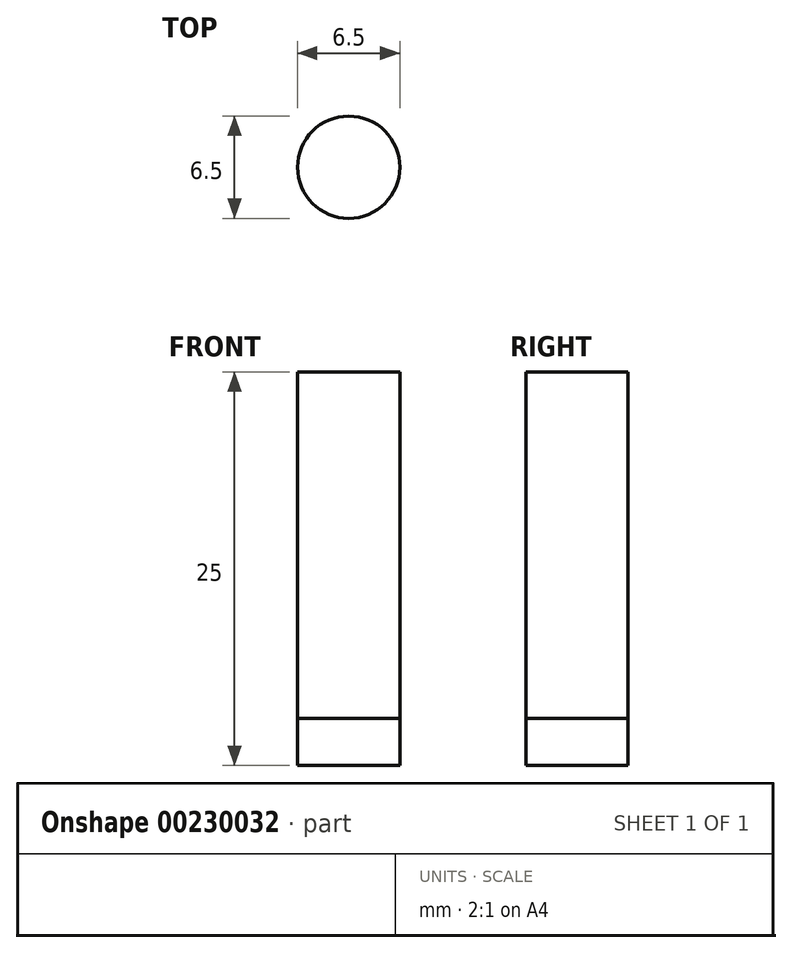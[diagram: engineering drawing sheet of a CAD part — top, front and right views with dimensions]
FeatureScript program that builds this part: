
annotation { "Feature Type Name" : "Feature", "Feature Type Description" : "" }
export const myFeature = defineFeature(function(context is Context, id is Id, definition is map)
    precondition{}
    {
        {
            var Q0;
            Q0=qCreatedBy(makeId("Top.planeOp"),FACE);
            var sketch = newSketch(context, id + "F0", { "sketchPlane" : qUnion([Q0])});
            skLineSegment(sketch, "E0", {"start": v(0, 0) * mm, "end": v(0, 7) * mm});
            skLineSegment(sketch, "E1", {"start": v(0, 7) * mm, "end": v(3, 7) * mm});
            skLineSegment(sketch, "E2", {"start": v(3, 7) * mm, "end": v(3, 17) * mm});
            skPoint(sketch, "E3.start.orphan", {"position": v(0, 17.47) * mm});
            skLineSegment(sketch, "E4", {"start": v(0, 17) * mm, "end": v(3, 17) * mm});
            skLineSegment(sketch, "E5", {"start": v(0, 17) * mm, "end": v(0, 24) * mm});
            skLineSegment(sketch, "E6", {"start": v(3, 24) * mm, "end": v(0, 24) * mm});
            skLineSegment(sketch, "E7", {"start": v(3, 24) * mm, "end": v(3, 34) * mm});
            skLineSegment(sketch, "E8", {"start": v(3, 34) * mm, "end": v(0, 34) * mm});
            skLineSegment(sketch, "E9", {"start": v(0, 34) * mm, "end": v(0, 41) * mm});
            skLineSegment(sketch, "E10", {"start": v(0, 41) * mm, "end": v(-17, 41) * mm});
            skLineSegment(sketch, "E11", {"start": v(-17, 44) * mm, "end": v(-17, 41) * mm});
            skLineSegment(sketch, "E12", {"start": v(-27, 44) * mm, "end": v(-17, 44) * mm});
            skLineSegment(sketch, "E13", {"start": v(-27, 41) * mm, "end": v(-27, 44) * mm});
            skLineSegment(sketch, "E14", {"start": v(-47, 41) * mm, "end": v(-27, 41) * mm});
            skLineSegment(sketch, "E15", {"start": v(-47, 41) * mm, "end": v(-47, 44) * mm});
            skLineSegment(sketch, "E16", {"start": v(-47, 44) * mm, "end": v(-57, 44) * mm});
            skLineSegment(sketch, "E17", {"start": v(-57, 44) * mm, "end": v(-57, 41) * mm});
            skLineSegment(sketch, "E18", {"start": v(-57, 41) * mm, "end": v(-77, 41) * mm});
            skLineSegment(sketch, "E19", {"start": v(-77, 41) * mm, "end": v(-77, 44) * mm});
            skLineSegment(sketch, "E20", {"start": v(-77, 44) * mm, "end": v(-87, 44) * mm});
            skLineSegment(sketch, "E21", {"start": v(-87, 44) * mm, "end": v(-87, 41) * mm});
            skLineSegment(sketch, "E22", {"start": v(-87, 41) * mm, "end": v(-104, 41) * mm});
            skLineSegment(sketch, "E23", {"start": v(-17, 0) * mm, "end": v(0, 0) * mm});
            skLineSegment(sketch, "E24", {"start": v(-17, -3) * mm, "end": v(-17, 0) * mm});
            skLineSegment(sketch, "E25", {"start": v(-27, -3) * mm, "end": v(-17, -3) * mm});
            skLineSegment(sketch, "E26", {"start": v(-27, 0) * mm, "end": v(-27, -3) * mm});
            skPoint(sketch, "E27.start.orphan", {"position": v(-47, 0) * mm});
            skLineSegment(sketch, "E28", {"start": v(-47, 0) * mm, "end": v(-27, 0) * mm});
            skLineSegment(sketch, "E29", {"start": v(-47, -3) * mm, "end": v(-47, 0) * mm});
            skLineSegment(sketch, "E30", {"start": v(-57, -3.09) * mm, "end": v(-47, -3) * mm});
            skPoint(sketch, "E31.start.orphan", {"position": v(-77, 0) * mm});
            skPoint(sketch, "E32.start.orphan", {"position": v(-57.64, 0) * mm});
            skPoint(sketch, "E33.start.orphan", {"position": v(-57.64, -3) * mm});
            skLineSegment(sketch, "E34", {"start": v(-57, 0) * mm, "end": v(-57.64, 0) * mm});
            skLineSegment(sketch, "E35", {"start": v(-57, 0) * mm, "end": v(-57, -3) * mm});
            skLineSegment(sketch, "E36", {"start": v(-57, 0) * mm, "end": v(-77, 0) * mm});
            skLineSegment(sketch, "E37", {"start": v(-77, -3.09) * mm, "end": v(-77, 0) * mm});
            skLineSegment(sketch, "E38", {"start": v(-87, -3) * mm, "end": v(-77, -3.09) * mm});
            skLineSegment(sketch, "E39", {"start": v(-87.03, 0) * mm, "end": v(-87, -3) * mm});
            skLineSegment(sketch, "E40", {"start": v(-104.03, 0) * mm, "end": v(-87.03, 0) * mm});
            skLineSegment(sketch, "E41", {"start": v(-104.03, 0) * mm, "end": v(-104.03, 7) * mm});
            skLineSegment(sketch, "E42", {"start": v(-104.03, 7) * mm, "end": v(-107.03, 7) * mm});
            skLineSegment(sketch, "E43", {"start": v(-107.03, 7) * mm, "end": v(-107.03, 17) * mm});
            skLineSegment(sketch, "E44", {"start": v(-107.03, 17) * mm, "end": v(-104.03, 17) * mm});
            skLineSegment(sketch, "E45", {"start": v(-104.03, 17) * mm, "end": v(-104.03, 24) * mm});
            skLineSegment(sketch, "E46", {"start": v(-104.03, 24) * mm, "end": v(-107.03, 24) * mm});
            skLineSegment(sketch, "E47", {"start": v(-107.03, 24) * mm, "end": v(-107.03, 34) * mm});
            skLineSegment(sketch, "E48", {"start": v(-107.03, 34) * mm, "end": v(-104, 34) * mm});
            skLineSegment(sketch, "E49", {"start": v(-104, 34) * mm, "end": v(-104, 41) * mm});
            skPoint(sketch, "E50.orphan", {"position": v(-104, 20.5) * mm});
            skPoint(sketch, "E51.start.orphan", {"position": v(0, 20.5) * mm});
            skPoint(sketch, "E52.end.orphan", {"position": v(-52, 44) * mm});
            skPoint(sketch, "E52.start.orphan", {"position": v(-52, -3.04) * mm});
            skCircle(sketch, "E53", {"center": v(-22.95, 25.29) * mm, "radius": 3.25 * mm});
            skSolve(sketch);
        }
        {
            var Q0;
            Q0 = qSketchRegion(id + "F0", true);
            extrude(context, id + "F1", {"entities" : qUnion([Q0]), "depth" : 25 * mm});
        }
        {
            var Q0;
            Q0 = qSketchRegion(id + "F0", true);
            extrude(context, id + "F2", {"entities" : qUnion([Q0]), "depth" : 3 * mm});
        }
        {
            var Q0;
            Q0 = qSketchRegion(id + "F0", true);
            extrude(context, id + "F3", {"entities" : qUnion([Q0]), "depth" : 3 * mm});
        }
    });
